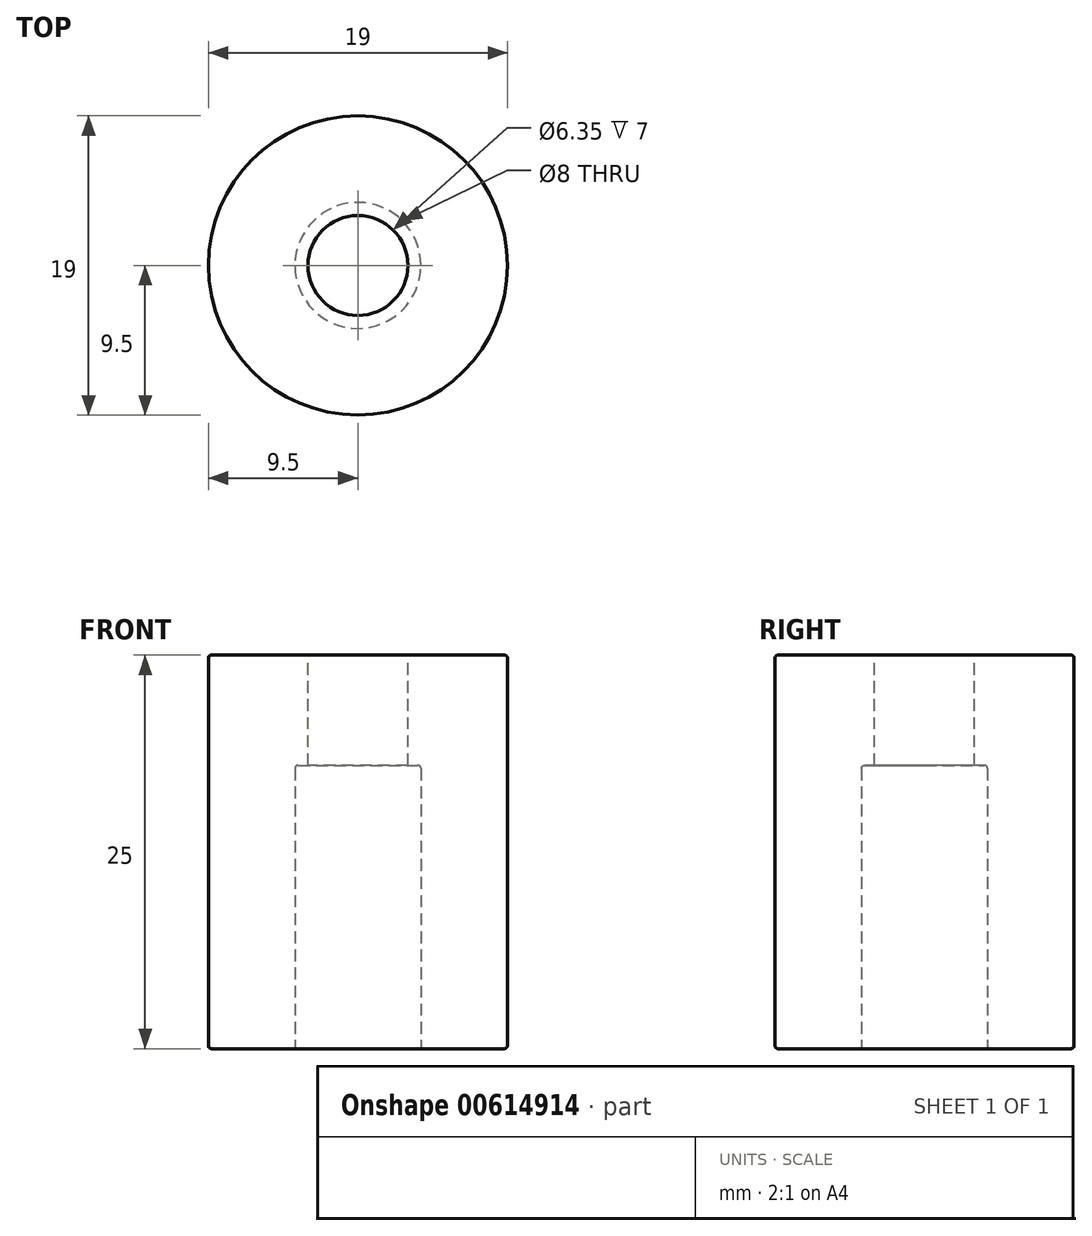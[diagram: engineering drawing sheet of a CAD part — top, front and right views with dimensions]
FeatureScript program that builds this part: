
annotation { "Feature Type Name" : "Feature", "Feature Type Description" : "" }
export const myFeature = defineFeature(function(context is Context, id is Id, definition is map)
    precondition{}
    {
        {
            var Q0;
            Q0=qCreatedBy(makeId("Top.planeOp"),FACE);
            var sketch = newSketch(context, id + "F0", { "sketchPlane" : qUnion([Q0])});
            skCircle(sketch, "E0", {"center": v(0, 0) * mm, "radius": 9.5 * mm});
            skSolve(sketch);
        }
        {
            var Q0;
            Q0 = qSketchRegion(id + "F0", true);
            extrude(context, id + "F1", {"entities" : qUnion([Q0]), "depth" : 25 * mm, "offsetDistance" : 25 * mm});
        }
        {
            var Q0;
            Q0=makeQuery(id+"F1.opExtrude","CAP_FACE",FACE,{"disambiguationData":[OSD([sQuery(id+"F0.wireOp",EDGE,"E0")])],"isStart":false});
            var sketch = newSketch(context, id + "F2", { "sketchPlane" : qUnion([Q0])});
            skCircle(sketch, "E1", {"center": v(0, 0) * mm, "radius": 3.18 * mm});
            skSolve(sketch);
        }
        {
            var Q0;
            Q0 = qSketchRegion(id + "F2", true);
            extrude(context, id + "F3", {"entities" : qUnion([Q0]), "operationType" : NewBodyOperationType.REMOVE, "oppositeDirection" : true, "depth" : 7 * mm, "offsetDistance" : 25 * mm});
        }
        {
            var Q0;
            Q0=makeQuery(id+"F1.opExtrude","CAP_FACE",FACE,{"disambiguationData":[OSD([sQuery(id+"F0.wireOp",EDGE,"E0")])],"isStart":true});
            var sketch = newSketch(context, id + "F4", { "sketchPlane" : qUnion([Q0])});
            skCircle(sketch, "E2", {"center": v(0, 0) * mm, "radius": 4 * mm});
            skSolve(sketch);
        }
        {
            var Q0;
            Q0 = qSketchRegion(id + "F4", true);
            extrude(context, id + "F5", {"entities" : qUnion([Q0]), "operationType" : NewBodyOperationType.REMOVE, "oppositeDirection" : true, "depth" : 18 * mm, "offsetDistance" : 25 * mm});
        }
        {
            var Q0;
            Q0=makeQuery(id+"F1.opExtrude","CAP_EDGE",EDGE,{"disambiguationData":[OSD([sQuery(id+"F0.wireOp",EDGE,"E0")])],"isStart":false});
            var Q1;
            Q1=makeQuery(id+"F1.opExtrude","CAP_EDGE",EDGE,{"disambiguationData":[OSD([sQuery(id+"F0.wireOp",EDGE,"E0")])],"isStart":true});
            var Q2;
            Q2=makeQuery(id+"F3.boolean.opBoolean","COPY",EDGE,{"derivedFrom":makeQuery(id+"F3.opExtrude","CAP_EDGE",EDGE,{"disambiguationData":[OSD([sQuery(id+"F2.wireOp",EDGE,"E1")])],"isStart":true})});
            var Q3;
            Q3=makeQuery(id+"F5.boolean.opBoolean","COPY",EDGE,{"derivedFrom":makeQuery(id+"F5.opExtrude","CAP_EDGE",EDGE,{"disambiguationData":[OSD([sQuery(id+"F4.wireOp",EDGE,"E2")])],"isStart":false})});
            var Q4;
            Q4=makeQuery(id+"F3.boolean.opBoolean","COPY",EDGE,{"derivedFrom":makeQuery(id+"F3.opExtrude","CAP_EDGE",EDGE,{"disambiguationData":[OSD([sQuery(id+"F2.wireOp",EDGE,"E1")])],"isStart":false})});
            var Q5;
            Q5=makeQuery(id+"F5.boolean.opBoolean","COPY",EDGE,{"derivedFrom":makeQuery(id+"F5.opExtrude","CAP_EDGE",EDGE,{"disambiguationData":[OSD([sQuery(id+"F4.wireOp",EDGE,"E2")])],"isStart":true})});
            fillet(context, id + "F6", {"entities" : qUnion([Q0, Q1, Q2, Q3, Q4, Q5]), "radius" : 0.2 * mm, "tangentPropagation" : true, "allowEdgeOverflow" : false});
        }
    });
